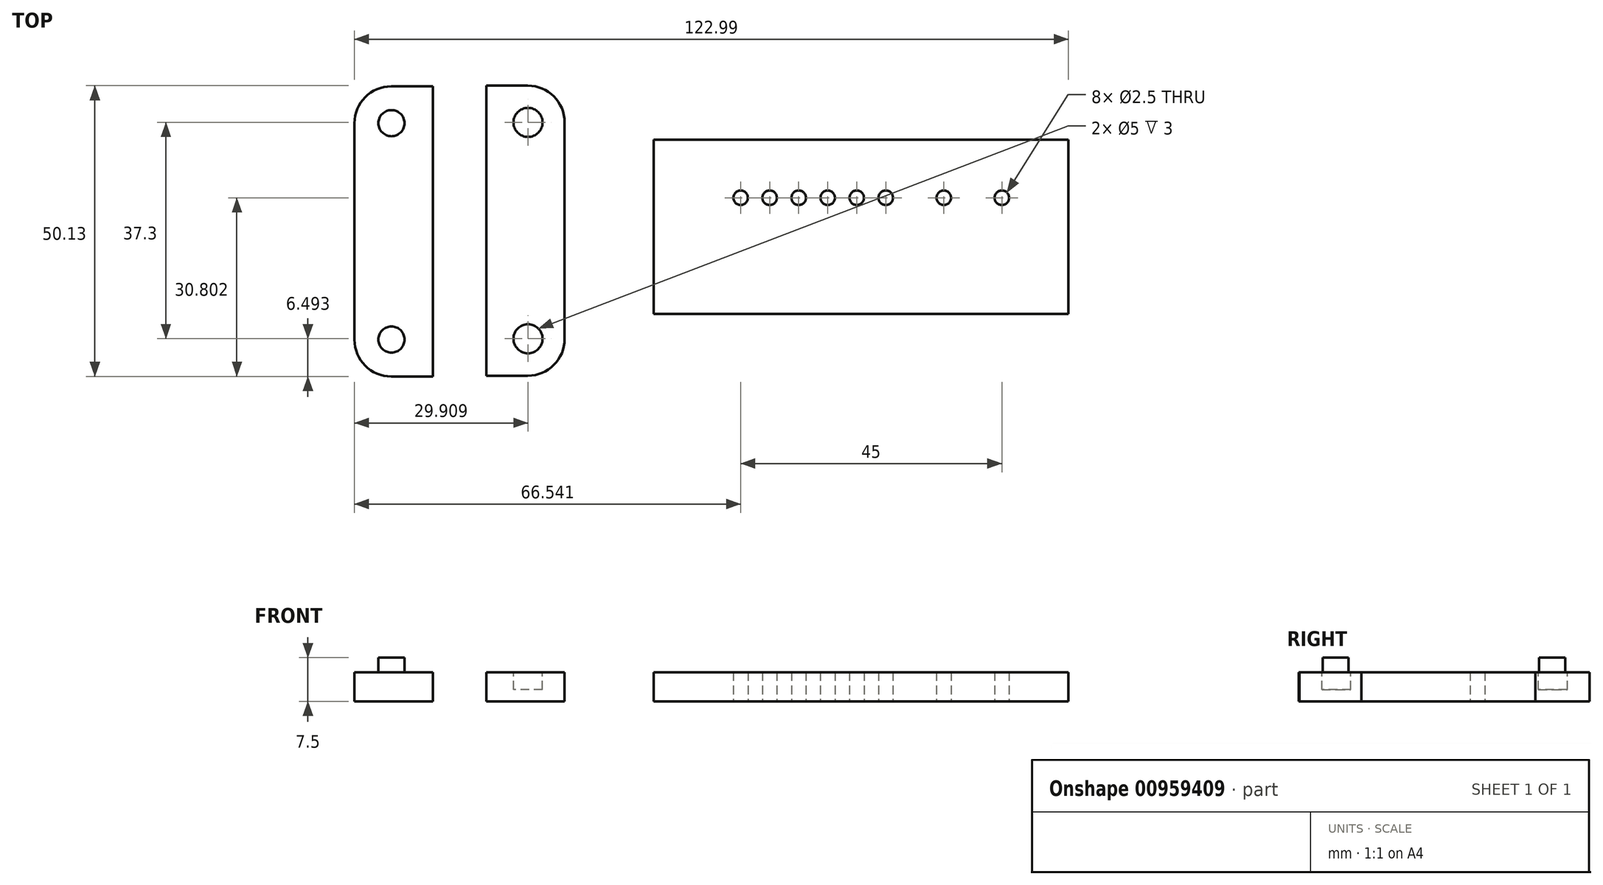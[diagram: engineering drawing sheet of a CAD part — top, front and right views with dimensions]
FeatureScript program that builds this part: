
annotation { "Feature Type Name" : "Feature", "Feature Type Description" : "" }
export const myFeature = defineFeature(function(context is Context, id is Id, definition is map)
    precondition{}
    {
        {
            var Q0;
            Q0=qCreatedBy(makeId("Top.planeOp"),FACE);
            var sketch = newSketch(context, id + "F0", { "sketchPlane" : qUnion([Q0])});
            skLineSegment(sketch, "E0.bottom", {"start": v(-83.55, 80.88) * mm, "end": v(-76.4, 80.88) * mm});
            skLineSegment(sketch, "E0.top", {"start": v(-83.55, 30.88) * mm, "end": v(-76.4, 30.88) * mm});
            skLineSegment(sketch, "E0.left", {"start": v(-89.9, 74.53) * mm, "end": v(-89.9, 37.23) * mm});
            skPoint(sketch, "E1.visualSharp", {"position": v(-89.9, 80.88) * mm});
            skArc(sketch, "E1.filletArc", {"start": v(-83.55, 80.88) * mm, "mid": v(-88.04, 79.02) * mm, "end": v(-89.9, 74.53) * mm});
            skPoint(sketch, "E2.visualSharp", {"position": v(-89.9, 30.88) * mm});
            skArc(sketch, "E2.filletArc", {"start": v(-89.9, 37.23) * mm, "mid": v(-88.04, 32.74) * mm, "end": v(-83.55, 30.88) * mm});
            skPoint(sketch, "E3.visualSharp", {"position": v(90.1, 80.88) * mm});
            skPoint(sketch, "E4.visualSharp", {"position": v(90.1, 30.88) * mm});
            skLineSegment(sketch, "E5", {"start": v(-76.4, 80.88) * mm, "end": v(-76.4, 30.88) * mm});
            skCircle(sketch, "E6", {"center": v(-83.55, 74.53) * mm, "radius": 2.25 * mm});
            skCircle(sketch, "E7", {"center": v(-83.55, 37.23) * mm, "radius": 2.25 * mm});
            skLineSegment(sketch, "E8.bottom", {"start": v(-60.03, 31.01) * mm, "end": v(-67.17, 31.01) * mm});
            skLineSegment(sketch, "E8.top", {"start": v(-60.03, 81.01) * mm, "end": v(-67.17, 81.01) * mm});
            skLineSegment(sketch, "E8.left", {"start": v(-53.68, 37.36) * mm, "end": v(-53.68, 74.66) * mm});
            skPoint(sketch, "E9.visualSharp", {"position": v(-53.68, 31.01) * mm});
            skArc(sketch, "E9.filletArc", {"start": v(-60.03, 31.01) * mm, "mid": v(-55.54, 32.87) * mm, "end": v(-53.68, 37.36) * mm});
            skPoint(sketch, "E10.visualSharp", {"position": v(-53.68, 81.01) * mm});
            skArc(sketch, "E10.filletArc", {"start": v(-53.68, 74.66) * mm, "mid": v(-55.54, 79.15) * mm, "end": v(-60.03, 81.01) * mm});
            skLineSegment(sketch, "E11", {"start": v(-67.17, 31.01) * mm, "end": v(-67.17, 81.01) * mm});
            skCircle(sketch, "E12", {"center": v(-60.03, 37.36) * mm, "radius": 2.5 * mm});
            skCircle(sketch, "E13", {"center": v(-60.03, 74.66) * mm, "radius": 2.5 * mm});
            skCircle(sketch, "E14", {"center": v(-23.36, 61.68) * mm, "radius": 1.25 * mm});
            skLineSegment(sketch, "E15", {"start": v(-38.36, 71.68) * mm, "end": v(-38.36, 41.68) * mm});
            skCircle(sketch, "E16", {"center": v(-18.36, 61.68) * mm, "radius": 1.25 * mm});
            skCircle(sketch, "E17", {"center": v(-13.36, 61.68) * mm, "radius": 1.25 * mm});
            skCircle(sketch, "E18", {"center": v(-8.36, 61.68) * mm, "radius": 1.25 * mm});
            skCircle(sketch, "E19", {"center": v(-3.36, 61.68) * mm, "radius": 1.25 * mm});
            skCircle(sketch, "E20", {"center": v(1.64, 61.68) * mm, "radius": 1.25 * mm});
            skCircle(sketch, "E21", {"center": v(11.64, 61.68) * mm, "radius": 1.25 * mm});
            skCircle(sketch, "E22", {"center": v(21.64, 61.68) * mm, "radius": 1.25 * mm});
            skLineSegment(sketch, "E23", {"start": v(-38.36, 71.68) * mm, "end": v(33.1, 71.68) * mm});
            skLineSegment(sketch, "E24", {"start": v(33.1, 71.68) * mm, "end": v(33.1, 41.68) * mm});
            skLineSegment(sketch, "E25", {"start": v(33.1, 41.68) * mm, "end": v(-38.36, 41.68) * mm});
            skPoint(sketch, "E26.center.orphan", {"position": v(16.64, 61.68) * mm});
            skPoint(sketch, "E27.center.orphan", {"position": v(6.64, 61.68) * mm});
            skSolve(sketch);
        }
        {
            var Q0;
            Q0=makeQuery(id+"F0.imprint","IMPRINT",FACE,{"disambiguationData":[TD([[makeQuery(id+"F0.imprint","IMPRINT",EDGE,{"derivedFrom":sQuery(id+"F0.wireOp",EDGE,"E0.bottom")}),-1.0]])]});
            var Q1;
            Q1=makeQuery(id+"F0.imprint","IMPRINT",FACE,{"disambiguationData":[TD([[makeQuery(id+"F0.imprint","IMPRINT",EDGE,{"derivedFrom":sQuery(id+"F0.wireOp",EDGE,"E6")}),1.0]])]});
            var Q2;
            Q2=makeQuery(id+"F0.imprint","IMPRINT",FACE,{"disambiguationData":[TD([[makeQuery(id+"F0.imprint","IMPRINT",EDGE,{"derivedFrom":sQuery(id+"F0.wireOp",EDGE,"E7")}),1.0]])]});
            var Q3;
            Q3=makeQuery(id+"F0.imprint","IMPRINT",FACE,{"disambiguationData":[TD([[makeQuery(id+"F0.imprint","IMPRINT",EDGE,{"derivedFrom":sQuery(id+"F0.wireOp",EDGE,"E12")}),1.0]])]});
            var Q4;
            Q4=makeQuery(id+"F0.imprint","IMPRINT",FACE,{"disambiguationData":[TD([[makeQuery(id+"F0.imprint","IMPRINT",EDGE,{"derivedFrom":sQuery(id+"F0.wireOp",EDGE,"E8.bottom")}),-1.0]])]});
            var Q5;
            Q5=makeQuery(id+"F0.imprint","IMPRINT",FACE,{"disambiguationData":[TD([[makeQuery(id+"F0.imprint","IMPRINT",EDGE,{"derivedFrom":sQuery(id+"F0.wireOp",EDGE,"E13")}),1.0]])]});
            var Q6;
            Q6=makeQuery(id+"F0.imprint","IMPRINT",FACE,{"disambiguationData":[TD([[makeQuery(id+"F0.imprint","IMPRINT",EDGE,{"derivedFrom":sQuery(id+"F0.wireOp",EDGE,"E14")}),-1.0]])]});
            extrude(context, id + "F1", {"entities" : qUnion([Q0, Q1, Q2, Q3, Q4, Q5, Q6]), "depth" : 5 * mm, "offsetDistance" : 25.4 * mm});
        }
        {
            var Q0;
            Q0=makeQuery(id+"F1.opExtrude","CAP_FACE",FACE,{"disambiguationData":[OSD([sQuery(id+"F0.wireOp",EDGE,"E0.bottom"),sQuery(id+"F0.wireOp",EDGE,"E0.top"),sQuery(id+"F0.wireOp",EDGE,"E0.left"),sQuery(id+"F0.wireOp",EDGE,"E1.filletArc"),sQuery(id+"F0.wireOp",EDGE,"E2.filletArc"),sQuery(id+"F0.wireOp",EDGE,"E5")])],"isStart":false});
            var sketch = newSketch(context, id + "F2", { "sketchPlane" : qUnion([Q0])});
            skLineSegment(sketch, "E28.bottom", {"start": v(-83.5, 80.9) * mm, "end": v(-76.36, 80.9) * mm});
            skLineSegment(sketch, "E28.top", {"start": v(-83.5, 30.9) * mm, "end": v(-76.36, 30.9) * mm});
            skLineSegment(sketch, "E28.left", {"start": v(-89.86, 74.54) * mm, "end": v(-89.86, 37.24) * mm});
            skPoint(sketch, "E29.visualSharp", {"position": v(-89.86, 80.9) * mm});
            skArc(sketch, "E29.filletArc", {"start": v(-83.5, 80.9) * mm, "mid": v(-88, 79.03) * mm, "end": v(-89.86, 74.54) * mm});
            skPoint(sketch, "E30.visualSharp", {"position": v(-89.86, 30.9) * mm});
            skArc(sketch, "E30.filletArc", {"start": v(-89.86, 37.24) * mm, "mid": v(-88, 32.75) * mm, "end": v(-83.5, 30.9) * mm});
            skLineSegment(sketch, "E31", {"start": v(-76.36, 80.9) * mm, "end": v(-76.36, 30.9) * mm});
            skCircle(sketch, "E32", {"center": v(-83.5, 74.54) * mm, "radius": 2.25 * mm});
            skCircle(sketch, "E33", {"center": v(-83.5, 37.24) * mm, "radius": 2.25 * mm});
            skLineSegment(sketch, "E34.bottom", {"start": v(-60, 31.02) * mm, "end": v(-67.14, 31.02) * mm});
            skLineSegment(sketch, "E34.top", {"start": v(-60, 81.02) * mm, "end": v(-67.14, 81.02) * mm});
            skLineSegment(sketch, "E34.left", {"start": v(-53.64, 37.37) * mm, "end": v(-53.64, 74.67) * mm});
            skPoint(sketch, "E35.visualSharp", {"position": v(-53.64, 31.02) * mm});
            skArc(sketch, "E35.filletArc", {"start": v(-60, 31.02) * mm, "mid": v(-55.5, 32.88) * mm, "end": v(-53.64, 37.37) * mm});
            skPoint(sketch, "E36.visualSharp", {"position": v(-53.64, 81.02) * mm});
            skArc(sketch, "E36.filletArc", {"start": v(-53.64, 74.67) * mm, "mid": v(-55.5, 79.16) * mm, "end": v(-60, 81.02) * mm});
            skLineSegment(sketch, "E37", {"start": v(-67.14, 31.02) * mm, "end": v(-67.14, 81.02) * mm});
            skCircle(sketch, "E38", {"center": v(-60, 37.37) * mm, "radius": 2.5 * mm});
            skCircle(sketch, "E39", {"center": v(-60, 74.67) * mm, "radius": 2.5 * mm});
            skSolve(sketch);
        }
        {
            var Q0;
            Q0=makeQuery(id+"F2.imprint","IMPRINT",FACE,{"disambiguationData":[TD([[makeQuery(id+"F2.imprint","IMPRINT",EDGE,{"derivedFrom":sQuery(id+"F2.wireOp",EDGE,"E32")}),1.0]])]});
            var Q1;
            Q1=makeQuery(id+"F2.imprint","IMPRINT",FACE,{"disambiguationData":[TD([[makeQuery(id+"F2.imprint","IMPRINT",EDGE,{"derivedFrom":sQuery(id+"F2.wireOp",EDGE,"E33")}),1.0]])]});
            extrude(context, id + "F3", {"entities" : qUnion([Q0, Q1]), "depth" : 2.5 * mm, "offsetDistance" : 25.4 * mm});
        }
        {
            var Q0;
            Q0=makeQuery(id+"F2.imprint","IMPRINT",FACE,{"disambiguationData":[TD([[makeQuery(id+"F2.imprint","IMPRINT",EDGE,{"derivedFrom":sQuery(id+"F2.wireOp",EDGE,"E39")}),1.0]])]});
            var Q1;
            Q1=makeQuery(id+"F2.imprint","IMPRINT",FACE,{"disambiguationData":[TD([[makeQuery(id+"F2.imprint","IMPRINT",EDGE,{"derivedFrom":sQuery(id+"F2.wireOp",EDGE,"E38")}),1.0]])]});
            extrude(context, id + "F4", {"entities" : qUnion([Q0, Q1]), "operationType" : NewBodyOperationType.REMOVE, "oppositeDirection" : true, "depth" : 3 * mm, "offsetDistance" : 25.4 * mm});
        }
    });
